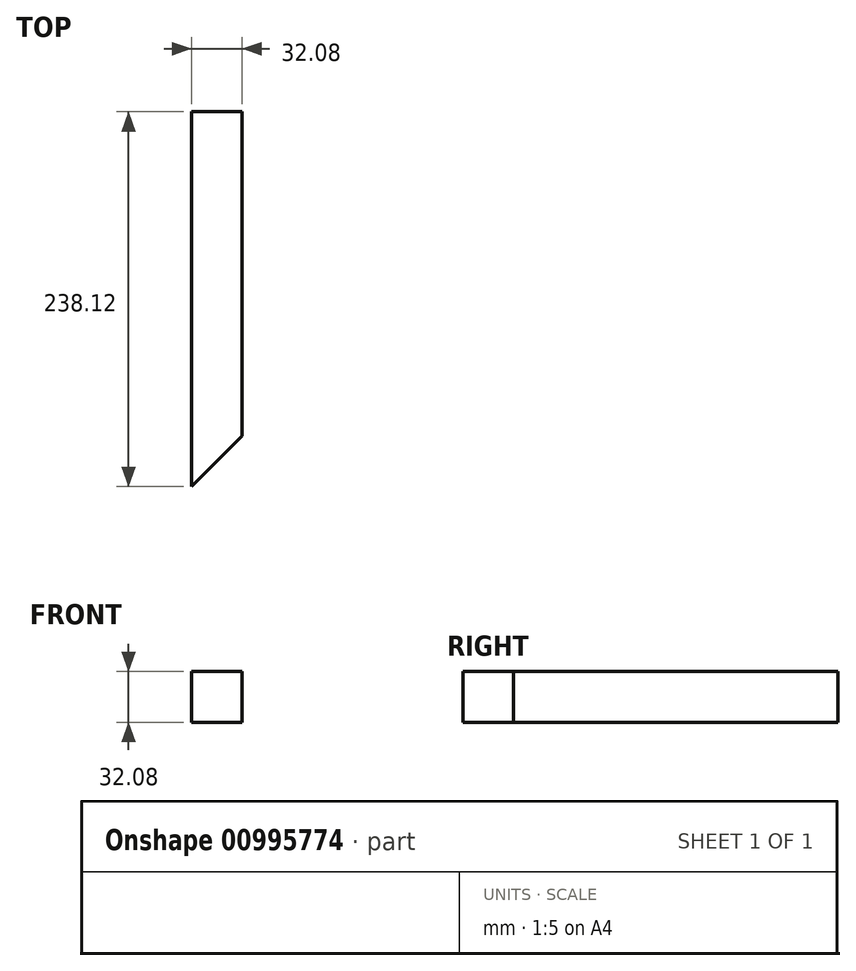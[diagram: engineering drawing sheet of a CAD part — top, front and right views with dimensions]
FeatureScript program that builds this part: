
annotation { "Feature Type Name" : "Feature", "Feature Type Description" : "" }
export const myFeature = defineFeature(function(context is Context, id is Id, definition is map)
    precondition{}
    {
        {
            var Q0;
            Q0=qCreatedBy(makeId("Top.planeOp"),FACE);
            var sketch = newSketch(context, id + "F0", { "sketchPlane" : qUnion([Q0])});
            skLineSegment(sketch, "E0.bottom", {"start": v(16.04, 119.06) * mm, "end": v(-16.04, 119.06) * mm});
            skLineSegment(sketch, "E0.top", {"start": v(16.04, -119.06) * mm, "end": v(-16.04, -119.06) * mm});
            skLineSegment(sketch, "E0.left", {"start": v(16.04, 119.06) * mm, "end": v(16.04, -119.06) * mm});
            skLineSegment(sketch, "E0.right", {"start": v(-16.04, 119.06) * mm, "end": v(-16.04, -119.06) * mm});
            skPoint(sketch, "E0.middle", {"position": v(0, 0) * mm});
            skSolve(sketch);
        }
        {
            var Q0;
            Q0=makeQuery(id+"F0.imprint","IMPRINT",FACE,{"disambiguationData":[TD([[makeQuery(id+"F0.imprint","IMPRINT",EDGE,{"derivedFrom":sQuery(id+"F0.wireOp",EDGE,"E0.bottom")}),1.0]])]});
            extrude(context, id + "F1", {"entities" : qUnion([Q0]), "endBound" : BoundingType.SYMMETRIC, "depth" : 32.08 * mm, "offsetDistance" : 25.4 * mm});
        }
        {
            var Q0;
            Q0=makeQuery(id+"F1.opExtrude","CAP_FACE",FACE,{"disambiguationData":[OSD([sQuery(id+"F0.wireOp",EDGE,"E0.bottom"),sQuery(id+"F0.wireOp",EDGE,"E0.top"),sQuery(id+"F0.wireOp",EDGE,"E0.left"),sQuery(id+"F0.wireOp",EDGE,"E0.right")])],"isStart":false});
            var sketch = newSketch(context, id + "F2", { "sketchPlane" : qUnion([Q0])});
            skLineSegment(sketch, "E1", {"start": v(16.04, -119.06) * mm, "end": v(16.04, -86.98) * mm});
            skLineSegment(sketch, "E2", {"start": v(16.04, -86.98) * mm, "end": v(-16.04, -119.06) * mm});
            skLineSegment(sketch, "E3", {"start": v(-16.04, -119.06) * mm, "end": v(16.04, -119.06) * mm});
            skSolve(sketch);
        }
        {
            var Q0;
            Q0 = qSketchRegion(id + "F2", true);
            extrude(context, id + "F3", {"entities" : qUnion([Q0]), "operationType" : NewBodyOperationType.REMOVE, "endBound" : BoundingType.UP_TO_NEXT, "oppositeDirection" : true, "depth" : 25.4 * mm, "offsetDistance" : 25.4 * mm});
        }
    });
